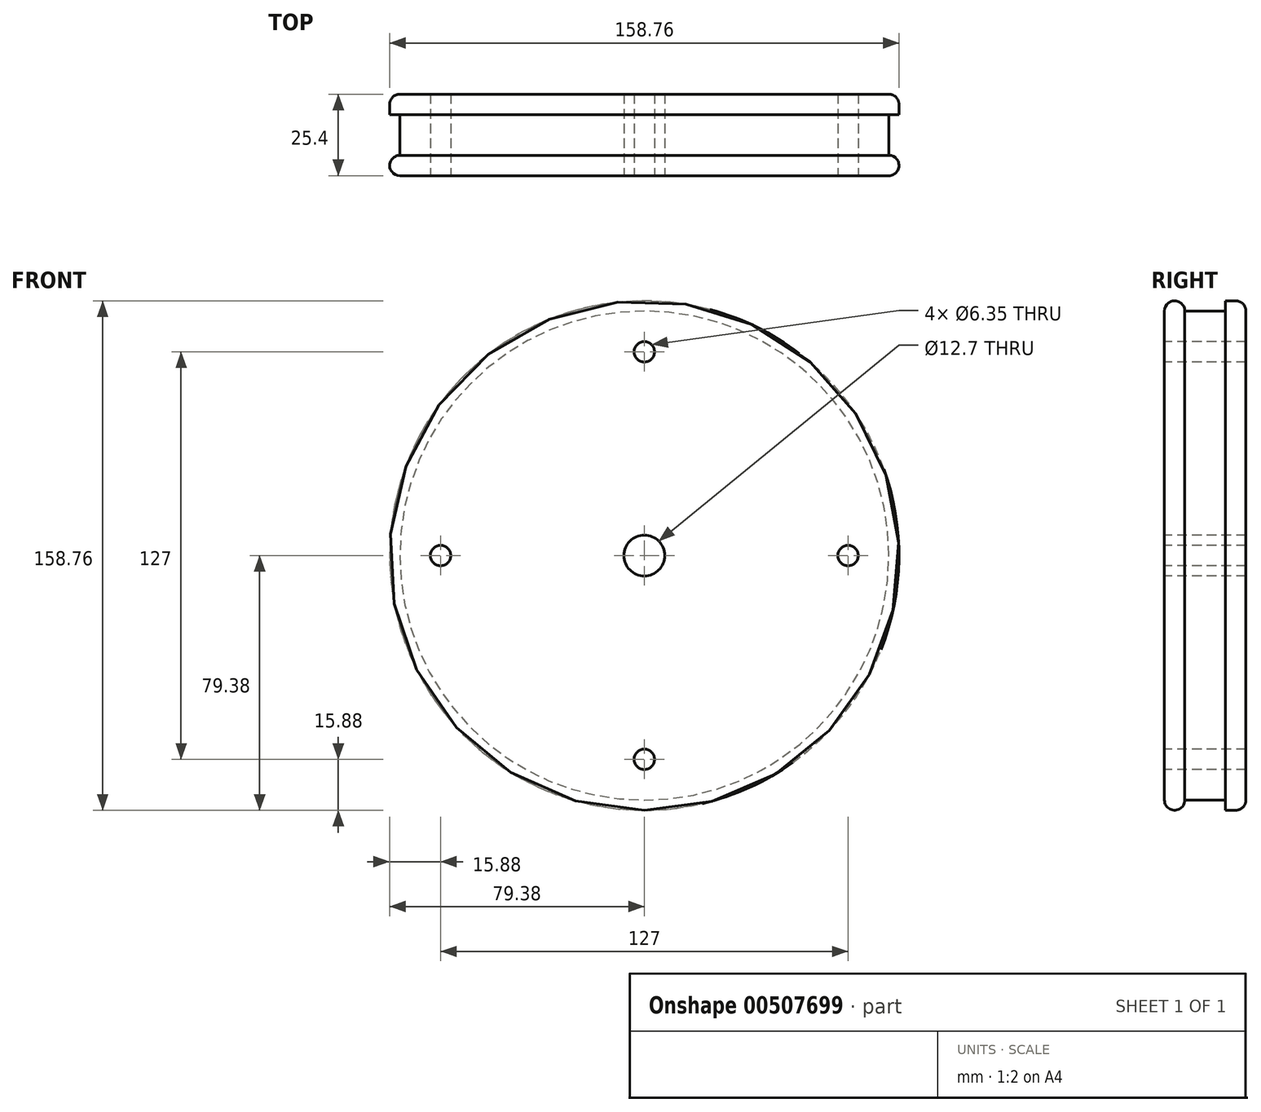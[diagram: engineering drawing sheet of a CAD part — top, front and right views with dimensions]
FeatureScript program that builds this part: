
annotation { "Feature Type Name" : "Feature", "Feature Type Description" : "" }
export const myFeature = defineFeature(function(context is Context, id is Id, definition is map)
    precondition{}
    {
        {
            var Q0;
            Q0=qCreatedBy(makeId("Front.planeOp"),FACE);
            var sketch = newSketch(context, id + "F0", { "sketchPlane" : qUnion([Q0])});
            skCircle(sketch, "E0", {"center": v(0, 0) * mm, "radius": 79.37 * mm});
            skSolve(sketch);
        }
        {
            var Q0;
            Q0=makeQuery(id+"F0.imprint","IMPRINT",FACE,{"disambiguationData":[TD([[makeQuery(id+"F0.imprint","IMPRINT",EDGE,{"derivedFrom":sQuery(id+"F0.wireOp",EDGE,"E0")}),1.0]])]});
            extrude(context, id + "F1", {"entities" : qUnion([Q0]), "depth" : 6.35 * mm, "offsetDistance" : 25.4 * mm});
        }
        {
            var Q0;
            Q0=makeQuery(id+"F1.opExtrude","CAP_FACE",FACE,{"disambiguationData":[OSD([sQuery(id+"F0.wireOp",EDGE,"E0")])],"isStart":false});
            var sketch = newSketch(context, id + "F2", { "sketchPlane" : qUnion([Q0])});
            skCircle(sketch, "E1", {"center": v(0, 0) * mm, "radius": 76.2 * mm});
            skSolve(sketch);
        }
        {
            var Q0;
            Q0 = qSketchRegion(id + "F2", true);
            extrude(context, id + "F3", {"entities" : qUnion([Q0]), "operationType" : NewBodyOperationType.ADD, "depth" : 12.7 * mm, "offsetDistance" : 25.4 * mm});
        }
        {
            var Q0;
            Q0=makeQuery(id+"F3.opExtrude","CAP_FACE",FACE,{"disambiguationData":[OSD([sQuery(id+"F2.wireOp",EDGE,"E1")])],"isStart":false});
            var sketch = newSketch(context, id + "F4", { "sketchPlane" : qUnion([Q0])});
            skCircle(sketch, "E2", {"center": v(0, 0) * mm, "radius": 79.38 * mm});
            skSolve(sketch);
        }
        {
            var Q0;
            Q0 = qSketchRegion(id + "F4", true);
            extrude(context, id + "F5", {"entities" : qUnion([Q0]), "operationType" : NewBodyOperationType.ADD, "depth" : 6.35 * mm, "offsetDistance" : 25.4 * mm});
        }
        {
            var Q0;
            Q0=makeQuery(id+"F5.opExtrude","CAP_EDGE",EDGE,{"disambiguationData":[OSD([sQuery(id+"F4.wireOp",EDGE,"E2")])],"isStart":false});
            var Q1;
            Q1=makeQuery(id+"F5.opExtrude","CAP_EDGE",EDGE,{"disambiguationData":[OSD([sQuery(id+"F4.wireOp",EDGE,"E2")])],"isStart":true});
            var Q2;
            Q2=makeQuery(id+"F1.opExtrude","CAP_EDGE",EDGE,{"disambiguationData":[OSD([sQuery(id+"F0.wireOp",EDGE,"E0")])],"isStart":true});
            var Q3;
            Q3=makeQuery(id+"F3.opExtrude","CAP_EDGE",EDGE,{"disambiguationData":[OSD([sQuery(id+"F2.wireOp",EDGE,"E1")])],"isStart":true});
            fillet(context, id + "F6", {"entities" : qUnion([Q0, Q1, Q2, Q3]), "radius" : 3.17 * mm, "tangentPropagation" : true, "allowEdgeOverflow" : false});
        }
        {
            var Q0;
            Q0=makeQuery(id+"F5.opExtrude","CAP_FACE",FACE,{"disambiguationData":[OSD([sQuery(id+"F4.wireOp",EDGE,"E2")])],"isStart":false});
            var sketch = newSketch(context, id + "F7", { "sketchPlane" : qUnion([Q0])});
            skPoint(sketch, "E3", {"position": v(0, 63.5) * mm});
            skPoint(sketch, "E4", {"position": v(63.5, 0) * mm});
            skPoint(sketch, "E5", {"position": v(-63.5, 0) * mm});
            skPoint(sketch, "E6", {"position": v(0, -63.5) * mm});
            skSolve(sketch);
        }
        {
            var Q0;
            Q0=sQuery(id+"F7.wireOp",VERTEX,"E3");
            var Q1;
            Q1=sQuery(id+"F7.wireOp",VERTEX,"E5");
            var Q2;
            Q2=sQuery(id+"F7.wireOp",VERTEX,"E6");
            var Q3;
            Q3=sQuery(id+"F7.wireOp",VERTEX,"E4");
            var Q4;
            Q4=makeQuery(id+"F1.opExtrude","SWEPT_BODY",BODY,{"disambiguationData":[OSD([sQuery(id+"F0.wireOp",EDGE,"E0")])]});
            hole(context, id + "F8", {"style" : HoleStyle.SIMPLE, "endStyle" : HoleEndStyle.THROUGH, "holeDiameter" : 6.35 * mm, "isTappedThrough" : true, "tappedDepth" : 12.7 * mm, "tapClearance" : 3, "locations" : qUnion([Q0, Q1, Q2, Q3]), "scope" : qUnion([Q4])});
        }
        {
            var Q0;
            Q0=makeQuery(id+"F5.opExtrude","CAP_FACE",FACE,{"disambiguationData":[OSD([sQuery(id+"F4.wireOp",EDGE,"E2")])],"isStart":false});
            var sketch = newSketch(context, id + "F9", { "sketchPlane" : qUnion([Q0])});
            skPoint(sketch, "E7", {"position": v(0, 0) * mm});
            skSolve(sketch);
        }
        {
            var Q0;
            Q0=sQuery(id+"F9.wireOp",VERTEX,"E7");
            var Q1;
            Q1=makeQuery(id+"F1.opExtrude","SWEPT_BODY",BODY,{"disambiguationData":[OSD([sQuery(id+"F0.wireOp",EDGE,"E0")])]});
            hole(context, id + "F10", {"style" : HoleStyle.SIMPLE, "endStyle" : HoleEndStyle.THROUGH, "holeDiameter" : 12.7 * mm, "isTappedThrough" : true, "tappedDepth" : 12.7 * mm, "tapClearance" : 3, "locations" : qUnion([Q0]), "scope" : qUnion([Q1])});
        }
    });
